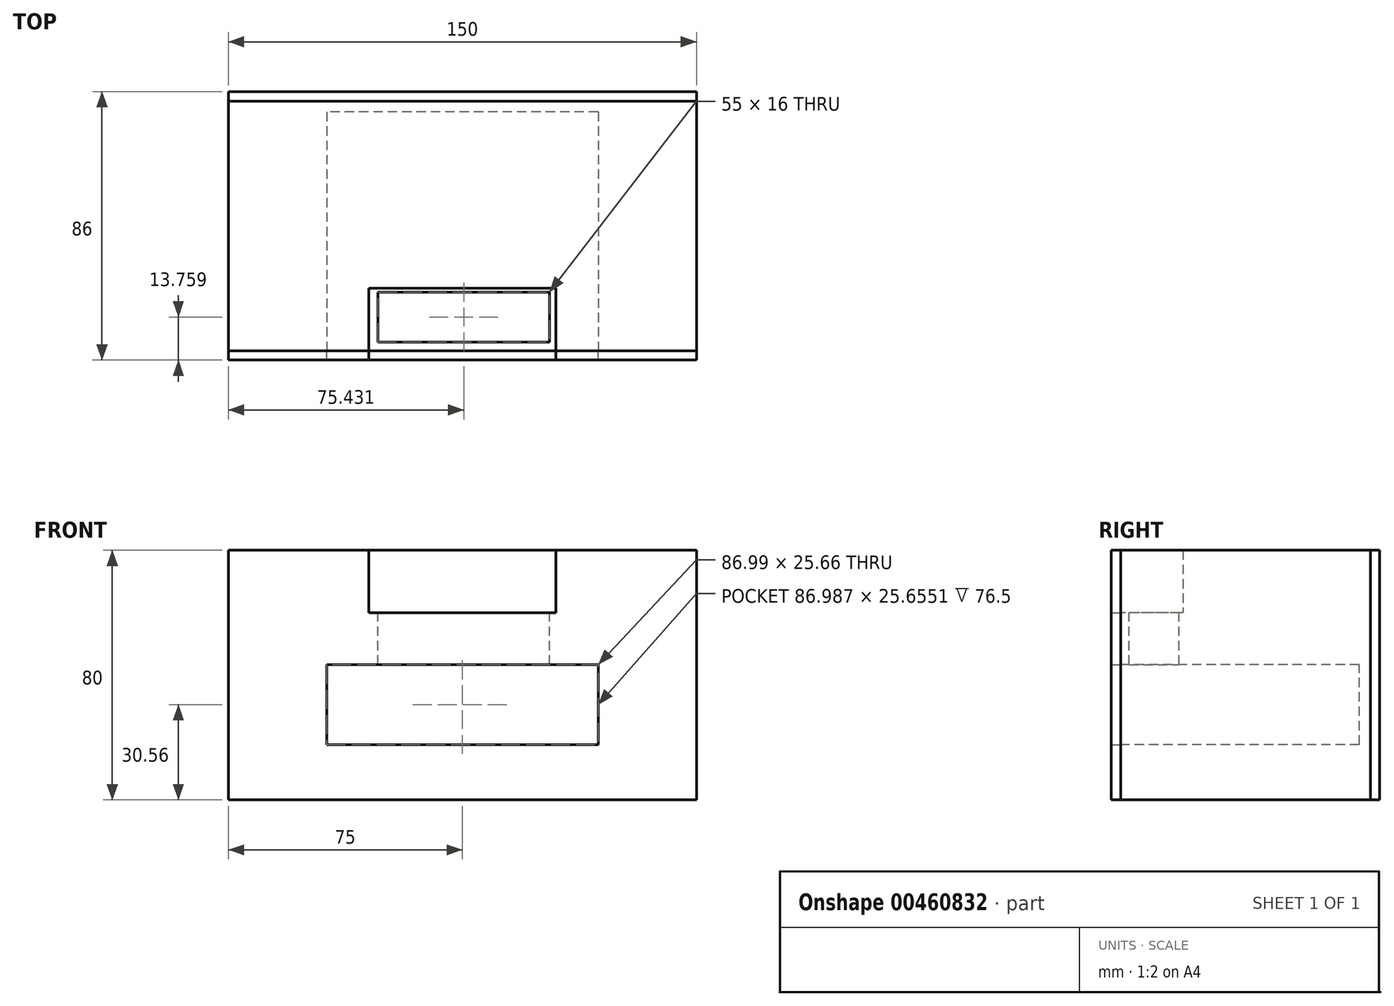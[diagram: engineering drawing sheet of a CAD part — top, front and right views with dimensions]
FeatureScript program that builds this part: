
annotation { "Feature Type Name" : "Feature", "Feature Type Description" : "" }
export const myFeature = defineFeature(function(context is Context, id is Id, definition is map)
    precondition{}
    {
        {
            var Q0;
            Q0=qCreatedBy(makeId("Top.planeOp"),FACE);
            var sketch = newSketch(context, id + "F0", { "sketchPlane" : qUnion([Q0])});
            skLineSegment(sketch, "E0.bottom", {"start": v(75, -40) * mm, "end": v(-75, -40) * mm});
            skLineSegment(sketch, "E0.top", {"start": v(75, 40) * mm, "end": v(-75, 40) * mm});
            skLineSegment(sketch, "E0.left", {"start": v(75, -40) * mm, "end": v(75, 40) * mm});
            skLineSegment(sketch, "E0.right", {"start": v(-75, -40) * mm, "end": v(-75, 40) * mm});
            skPoint(sketch, "E0.middle", {"position": v(0, 0) * mm});
            skSolve(sketch);
        }
        {
            var Q0;
            Q0 = qSketchRegion(id + "F0", true);
            extrude(context, id + "F1", {"entities" : qUnion([Q0]), "depth" : 80 * mm});
        }
        {
            var Q0;
            Q0=makeQuery(id+"F1.opExtrude","SWEPT_FACE",FACE,{"disambiguationData":[OSD([sQuery(id+"F0.wireOp",EDGE,"E0.bottom")])]});
            var sketch = newSketch(context, id + "F2", { "sketchPlane" : qUnion([Q0])});
            skLineSegment(sketch, "E1.bottom", {"start": v(-30, 80) * mm, "end": v(30, 80) * mm});
            skLineSegment(sketch, "E1.top", {"start": v(-30, 60) * mm, "end": v(30, 60) * mm});
            skLineSegment(sketch, "E1.left", {"start": v(-30, 80) * mm, "end": v(-30, 60) * mm});
            skLineSegment(sketch, "E1.right", {"start": v(30, 80) * mm, "end": v(30, 60) * mm});
            skLineSegment(sketch, "E2", {"start": v(0, 60) * mm, "end": v(0, 80) * mm});
            skSolve(sketch);
        }
        {
            var Q0;
            {var subQ0=sQuery(id+"F2.wireOp",EDGE,"E1.right");Q0=makeQuery(id+"F2.imprint","IMPRINT",FACE,{"disambiguationData":[TD([[makeQuery(id+"F2.imprint","IMPRINT",EDGE,{"derivedFrom":subQ0}),-1.0]])]});}
            var Q1;
            {var subQ0=sQuery(id+"F2.wireOp",EDGE,"E1.left");Q1=makeQuery(id+"F2.imprint","IMPRINT",FACE,{"disambiguationData":[TD([[makeQuery(id+"F2.imprint","IMPRINT",EDGE,{"derivedFrom":subQ0}),1.0]])]});}
            extrude(context, id + "F3", {"entities" : qUnion([Q0, Q1]), "operationType" : NewBodyOperationType.REMOVE, "oppositeDirection" : true, "depth" : 20 * mm});
        }
        {
            var Q0;
            Q0=makeQuery(id+"F3.boolean.opBoolean","COPY",FACE,{"derivedFrom":makeQuery(id+"F3.opExtrude","SWEPT_FACE",FACE,{"disambiguationData":[OSD([sQuery(id+"F2.wireOp",EDGE,"E1.top")])]})});
            var sketch = newSketch(context, id + "F4", { "sketchPlane" : qUnion([Q0])});
            skLineSegment(sketch, "E3.bottom", {"start": v(-27.07, -21.24) * mm, "end": v(27.93, -21.24) * mm});
            skLineSegment(sketch, "E3.top", {"start": v(-27.07, -37.24) * mm, "end": v(27.93, -37.24) * mm});
            skLineSegment(sketch, "E3.left", {"start": v(-27.07, -21.24) * mm, "end": v(-27.07, -37.24) * mm});
            skLineSegment(sketch, "E3.right", {"start": v(27.93, -21.24) * mm, "end": v(27.93, -37.24) * mm});
            skSolve(sketch);
        }
        {
            var Q0;
            Q0=makeQuery(id+"F4.imprint","IMPRINT",FACE,{"disambiguationData":[TD([[makeQuery(id+"F4.imprint","IMPRINT",EDGE,{"derivedFrom":sQuery(id+"F4.wireOp",EDGE,"E3.bottom")}),-1.0]])]});
            extrude(context, id + "F5", {"entities" : qUnion([Q0]), "operationType" : NewBodyOperationType.REMOVE, "oppositeDirection" : true, "depth" : 26.8 * mm});
        }
        {
            var Q0;
            Q0=makeQuery(id+"F1.opExtrude","SWEPT_FACE",FACE,{"disambiguationData":[OSD([sQuery(id+"F0.wireOp",EDGE,"E0.bottom")])]});
            var sketch = newSketch(context, id + "F6", { "sketchPlane" : qUnion([Q0])});
            skLineSegment(sketch, "E4.bottom", {"start": v(43.5, 17.73) * mm, "end": v(-43.5, 17.73) * mm});
            skLineSegment(sketch, "E4.top", {"start": v(43.5, 43.39) * mm, "end": v(-43.5, 43.39) * mm});
            skLineSegment(sketch, "E4.left", {"start": v(43.5, 17.73) * mm, "end": v(43.5, 43.39) * mm});
            skLineSegment(sketch, "E4.right", {"start": v(-43.5, 17.73) * mm, "end": v(-43.5, 43.39) * mm});
            skPoint(sketch, "E4.middle", {"position": v(0, 30.56) * mm});
            skSolve(sketch);
        }
        {
            var Q0;
            Q0 = qSketchRegion(id + "F6", true);
            extrude(context, id + "F7", {"entities" : qUnion([Q0]), "operationType" : NewBodyOperationType.REMOVE, "oppositeDirection" : true, "depth" : 76.5 * mm});
        }
        {
            var Q0;
            Q0=makeQuery(id+"F1.opExtrude","SWEPT_FACE",FACE,{"disambiguationData":[OSD([sQuery(id+"F0.wireOp",EDGE,"E0.bottom")])]});
            var sketch = newSketch(context, id + "F8", { "sketchPlane" : qUnion([Q0])});
            skLineSegment(sketch, "E5.bottom", {"start": v(75, 80) * mm, "end": v(-75, 80) * mm});
            skLineSegment(sketch, "E5.top", {"start": v(75, 0) * mm, "end": v(-75, 0) * mm});
            skLineSegment(sketch, "E5.left", {"start": v(75, 80) * mm, "end": v(75, 0) * mm});
            skLineSegment(sketch, "E5.right", {"start": v(-75, 80) * mm, "end": v(-75, 0) * mm});
            skSolve(sketch);
        }
        {
            var Q0;
            Q0=makeQuery(id+"F8.imprint","IMPRINT",FACE,{"disambiguationData":[TD([[makeQuery(id+"F8.imprint","IMPRINT",EDGE,{"derivedFrom":sQuery(id+"F8.wireOp",EDGE,"E5.top")}),-1.0]])]});
            extrude(context, id + "F9", {"entities" : qUnion([Q0]), "depth" : 3 * mm});
        }
        {
            var Q0;
            Q0=makeQuery(id+"F1.opExtrude","SWEPT_FACE",FACE,{"disambiguationData":[OSD([sQuery(id+"F0.wireOp",EDGE,"E0.top")])]});
            var sketch = newSketch(context, id + "F10", { "sketchPlane" : qUnion([Q0])});
            skLineSegment(sketch, "E6.bottom", {"start": v(-75, 80) * mm, "end": v(75, 80) * mm});
            skLineSegment(sketch, "E6.top", {"start": v(-75, 0) * mm, "end": v(75, 0) * mm});
            skLineSegment(sketch, "E6.left", {"start": v(-75, 80) * mm, "end": v(-75, 0) * mm});
            skLineSegment(sketch, "E6.right", {"start": v(75, 80) * mm, "end": v(75, 0) * mm});
            skSolve(sketch);
        }
        {
            var Q0;
            Q0=makeQuery(id+"F10.imprint","IMPRINT",FACE,{"disambiguationData":[TD([[makeQuery(id+"F10.imprint","IMPRINT",EDGE,{"derivedFrom":sQuery(id+"F10.wireOp",EDGE,"E6.bottom")}),-1.0]])]});
            extrude(context, id + "F11", {"entities" : qUnion([Q0]), "depth" : 3 * mm});
        }
    });
